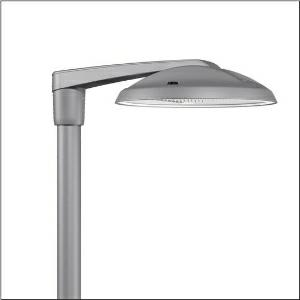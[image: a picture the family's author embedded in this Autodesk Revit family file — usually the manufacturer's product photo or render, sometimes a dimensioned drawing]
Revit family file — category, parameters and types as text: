
# Revit family: dl_50_iq_mini___st1_0a_5xa248d31v08me_a4b1
name_source: partatom
category: Lighting Fixtures
units: mm (PartAtom-declared; Revit-internal decimal feet)

## family parameters
Cut with Voids When Loaded = No
Host = Face
Light Source = No
Part Type = Normal
Room Calculation Point = No
Round Connector Dimension = Use Diameter
Shared = No

## types (1)
- --- (1 x LED, 15720 lm, 107 W, 3000K)
    Apparent Load = 107 VA
    CIE Flux Codes = 37 72 97 100 100
    Color Rendering = 70
    Color Temperature = 3000K
    Default Elevation = 1800 mm
    Description = DL 50 iQ mini, mast luminaire, primary light control with lens, of PMMA, primary optical cover: cover, of toughened safety glass, transparent, light distribution: ST1.0a, light emission: direct distribution, primary light characteristic: asymmetric, installation type: post-top, side-entry, LED, High Power LED, rated luminous flux: 15.720lm, luminous efficacy: 147lm/W, light colour: 730, colour temperature: 3000K, control gear: iQ-Street Remote, D4i with power reduction, control: optimised constant luminous flux control (CLO 2.0), Desk-Remote (wireless, voltage-free reading and setting of iQ features in the workshop via application-optimized NFC function/RFID function), Light-Fading, Smart-Wire, Night-Set, Lumen-Switch, Temp-Guard, Auto-Match, Street-Remote, pre-setting: logarithmic dimming characteristic, mains connection: 230..240V, AC, 50/60Hz, connection cable pre-assembled, cable length: 10,5m, start of lifetime: 107W, end of service life: 113W, reduction: 47W, luminaire housing, of diecast aluminium, powder-coated, SITECO metallic grey (DB 702S), inclination adjustable: 0°, 5°, 10° (post-top) | 0°, -5°, -10°, -15° (side-entry), please order mast post-top element or mast side-entry element separately, diameter: 500mm, height: 115mm, post-top: for spigot size d x l = 76 x 100mm; with reducer (optional accessory) 60 x 100mm | side-entry: for spigot size d x l = 60 x 100mm; with reducer (optional accessory) 42 x 100mm, mounting height: 4..6m, Smart Interface above, protection rating (complete): IP66, insulation class (complete): insulation class II (safety insulation), certification: CE, ENEC, ENEC+, VDE, impact resistance: IK08, permissible operating ambient temperature for outdoor applications: -25..+40°C, standard-compliant lighting for roads and squares, packaging unit: 1 piece

Light Distribution: ST1.0a
    Height = 115 mm
    Lamp = 1 x LED
    Lamp Light Flux = 15720 lm
    Lamp Power = 107 W
    Lamp count = 1
    Length = 500 mm
    Luminous efficacy = 147 lm/W
    Manufacturer = Siteco
    ModVariant = No
    Model = 5XA248D31V08ME
    Number of Poles = 1
    OnlyDefault = Yes
    Power Factor = 1
    Product Name = DL 50 iQ mini | ST1.0a
    Product group = mast luminaire | pylon top
    ProductGroupID = 6100
    Protection Class = Protection class II
    Protection Degree = IP 66
    RLX_Detail_Level = 1
    RLX_Emergency_Light_Flux = 0 lm
    RLX_Emergency_Type = 0
    RLX_Emergency_Type_DB = No
    RlxData = <blob elided: 106277 chars, md5=2bf47c48>
    Socket = socket
    Standby Power = 0 W
    System Light Flux = 15720 lm
    System Power = 107 W
    Type Comments = factory setting: luminous flux: 100 % | dim-lin: 254 | 565 mA
    Type Image = l_1251788.jpg
    URL = http://relux.com
    VarID = @adj_075115
    Voltage = 0 V
    Weight = 0.00 kg
    Width = 0 mm  [stored 0 ft]

note: [stored X ft] marks values corroborated as IEEE doubles in the binary element streams (Revit-internal decimal feet)

## geometry (parser evidence)
native form markers: Blend x4, Sweep x8
no freeform markers — native parametric forms only
